# Revit family: 35806-PRESTO
name_source: partatom
category: Plumbing Fixtures
units: mm (PartAtom-declared; Revit-internal decimal feet)

## family parameters
Always vertical = Yes
Cut with Voids When Loaded = No
Maintain Annotation Orientation = No
OmniClass Number = 23.45.00.00
OmniClass Title = Sanitary, Laundry, and Cleaning Equipment
Part Type = Normal
Room Calculation Point = No
Round Connector Dimension = Use Diameter
Shared = No
Work Plane-Based = Yes

## types (1)
- 35806- Les Robinets PRESTO
    BRAND = PRESTO
    DELEVER WITH = 2 Filter gaskets
    Default Elevation = 1219 mm
    Description = 2 Filter gaskets
    FLOW = 0.1 L/s
    MIN PRESSURE = 0.0 Pa
    Model = 35806
    PIPING SUP = 15.00 mm
    PRESSURE = 0.0 Pa
    RANGE = PRESTO 3500
    REF = 35806 - Single control wall-mounted mixer tap - Directional flow straightener
    SECURTIY = Adjustable tamper-proof temperature limiter to prevent scalding
    STANDARD = Brass body in accordance with EN 1982, EN 12164, EN 12156
Molded chrome-plated body in accordance with EN 12540
200-hour neutral salt spray resistant (NSS) in accordance with ISO 9227
    Thermal resistance = 75.0000 (m²·K)/W
    URL = https://www.prestodatashare.com
    brand = Les Robinets PRESTO
    material = Black push-button

## geometry (parser evidence)
native form markers: Sweep x2
no freeform markers — native parametric forms only
